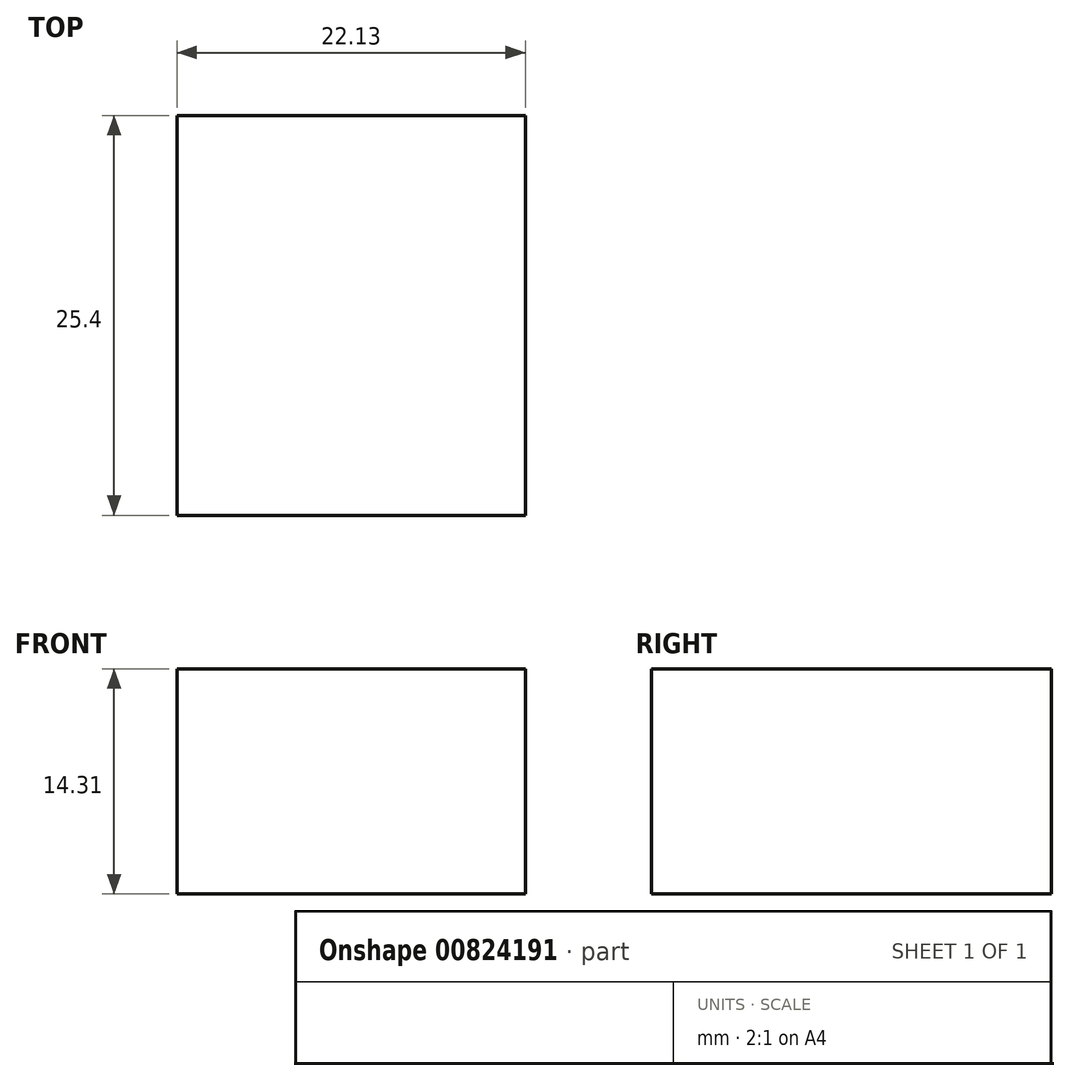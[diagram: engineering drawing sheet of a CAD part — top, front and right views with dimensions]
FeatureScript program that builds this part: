
annotation { "Feature Type Name" : "Feature", "Feature Type Description" : "" }
export const myFeature = defineFeature(function(context is Context, id is Id, definition is map)
    precondition{}
    {
        {
            var Q0;
            Q0=qCreatedBy(makeId("Front.planeOp"),FACE);
            var sketch = newSketch(context, id + "F0", { "sketchPlane" : qUnion([Q0])});
            skLineSegment(sketch, "E0.bottom", {"start": v(-74, 48.73) * mm, "end": v(-51.87, 48.73) * mm});
            skLineSegment(sketch, "E0.top", {"start": v(-74, 34.42) * mm, "end": v(-51.87, 34.42) * mm});
            skLineSegment(sketch, "E0.left", {"start": v(-74, 48.73) * mm, "end": v(-74, 34.42) * mm});
            skLineSegment(sketch, "E0.right", {"start": v(-51.87, 48.73) * mm, "end": v(-51.87, 34.42) * mm});
            skSolve(sketch);
        }
        {
            var Q0;
            Q0 = qSketchRegion(id + "F0", true);
            extrude(context, id + "F1", {"entities" : qUnion([Q0]), "depth" : 25.4 * mm, "offsetDistance" : 25.4 * mm});
        }
    });
